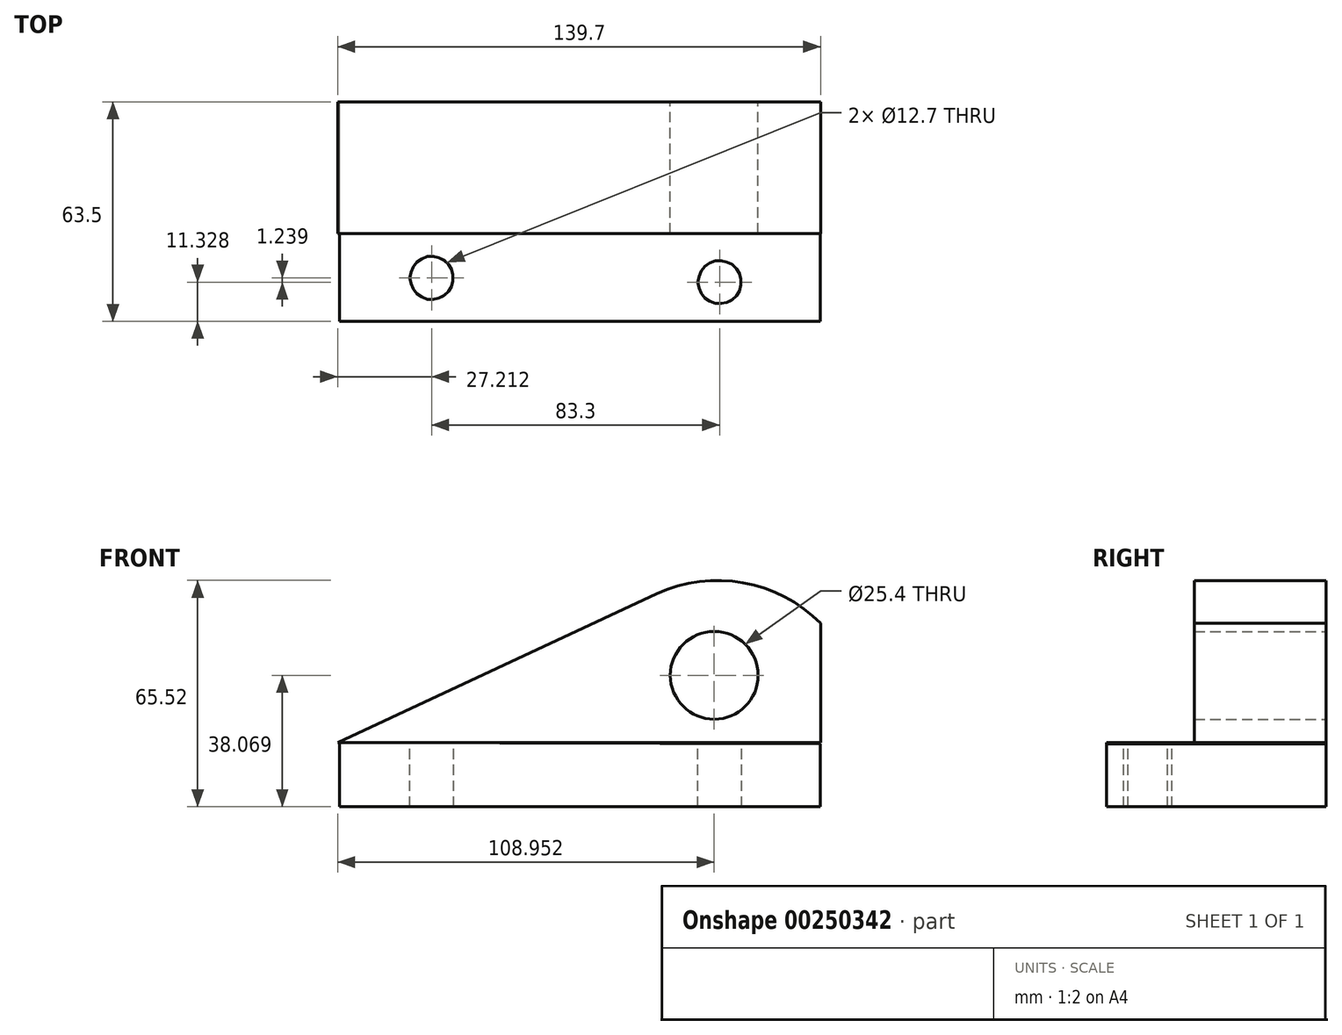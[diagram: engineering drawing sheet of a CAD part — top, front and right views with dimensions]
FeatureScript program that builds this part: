
annotation { "Feature Type Name" : "Feature", "Feature Type Description" : "" }
export const myFeature = defineFeature(function(context is Context, id is Id, definition is map)
    precondition{}
    {
        {
            var Q0;
            Q0=qCreatedBy(makeId("Front.planeOp"),FACE);
            var sketch = newSketch(context, id + "F0", { "sketchPlane" : qUnion([Q0])});
            skLineSegment(sketch, "E0", {"start": v(-73.3, -34.51) * mm, "end": v(66.4, -34.51) * mm});
            skLineSegment(sketch, "E1", {"start": v(66.4, -34.51) * mm, "end": v(66.4, 0) * mm});
            skLineSegment(sketch, "E2", {"start": v(-73.3, -34.51) * mm, "end": v(18.94, 8.51) * mm});
            skArc(sketch, "E3", {"start": v(66.4, 0) * mm, "mid": v(44.02, 11.78) * mm, "end": v(18.94, 8.51) * mm});
            skSolve(sketch);
        }
        {
            var Q0;
            Q0=qCreatedBy(makeId("Front.planeOp"),FACE);
            var sketch = newSketch(context, id + "F1", { "sketchPlane" : qUnion([Q0])});
            skLineSegment(sketch, "E4", {"start": v(66.3, -34.82) * mm, "end": v(66.3, -53.08) * mm});
            skLineSegment(sketch, "E5", {"start": v(66.3, -53.08) * mm, "end": v(-72.68, -53.08) * mm});
            skLineSegment(sketch, "E6", {"start": v(-72.68, -53.08) * mm, "end": v(-72.68, -34.51) * mm});
            skLineSegment(sketch, "E7", {"start": v(-72.68, -34.51) * mm, "end": v(66.3, -34.82) * mm});
            skSolve(sketch);
        }
        {
            var Q0;
            Q0=makeQuery(id+"F0.imprint","IMPRINT",FACE,{"disambiguationData":[TD([[makeQuery(id+"F0.imprint","IMPRINT",EDGE,{"derivedFrom":sQuery(id+"F0.wireOp",EDGE,"E0")}),1.0]])]});
            extrude(context, id + "F2", {"entities" : qUnion([Q0]), "depth" : 38.1 * mm});
        }
        {
            var Q0;
            Q0=makeQuery(id+"F1.imprint","IMPRINT",FACE,{"disambiguationData":[TD([[makeQuery(id+"F1.imprint","IMPRINT",EDGE,{"derivedFrom":sQuery(id+"F1.wireOp",EDGE,"E4")}),-1.0]])]});
            extrude(context, id + "F3", {"entities" : qUnion([Q0]), "depth" : 63.5 * mm});
        }
        {
            var Q0;
            Q0=qCreatedBy(makeId("Front.planeOp"),FACE);
            var sketch = newSketch(context, id + "F4", { "sketchPlane" : qUnion([Q0])});
            skLineSegment(sketch, "E8", {"start": v(35.65, -15.01) * mm, "end": v(10.9, -15.01) * mm});
            skSolve(sketch);
        }
        {
            var Q0;
            Q0=sQuery(id+"F4.wireOp",VERTEX,"E8.start");
            var Q1;
            Q1=makeQuery(id+"F2.opExtrude","SWEPT_BODY",BODY,{"disambiguationData":[OSD([sQuery(id+"F0.wireOp",EDGE,"E0"),sQuery(id+"F0.wireOp",EDGE,"E1"),sQuery(id+"F0.wireOp",EDGE,"E2"),sQuery(id+"F0.wireOp",EDGE,"E3")])]});
            hole(context, id + "F5", {"style" : HoleStyle.SIMPLE, "endStyle" : HoleEndStyle.THROUGH, "oppositeDirection" : true, "holeDiameter" : 25.4 * mm, "tappedDepth" : 12.7 * mm, "tapClearance" : 3, "locations" : qUnion([Q0]), "scope" : qUnion([Q1])});
        }
        {
            var Q0;
            Q0=qCreatedBy(makeId("Top.planeOp"),FACE);
            var sketch = newSketch(context, id + "F6", { "sketchPlane" : qUnion([Q0])});
            skLineSegment(sketch, "E9", {"start": v(-46.09, -50.93) * mm, "end": v(-64.98, -50.93) * mm});
            skSolve(sketch);
        }
        {
            var Q0;
            Q0=sQuery(id+"F6.wireOp",VERTEX,"E9.start");
            var Q1;
            Q1=makeQuery(id+"F3.opExtrude","SWEPT_BODY",BODY,{"disambiguationData":[OSD([sQuery(id+"F1.wireOp",EDGE,"E4"),sQuery(id+"F1.wireOp",EDGE,"E5"),sQuery(id+"F1.wireOp",EDGE,"E6"),sQuery(id+"F1.wireOp",EDGE,"E7")])]});
            hole(context, id + "F7", {"style" : HoleStyle.SIMPLE, "endStyle" : HoleEndStyle.THROUGH, "holeDiameter" : 12.7 * mm, "tappedDepth" : 12.7 * mm, "tapClearance" : 3, "locations" : qUnion([Q0]), "scope" : qUnion([Q1])});
        }
        {
            var Q0;
            Q0=qCreatedBy(makeId("Top.planeOp"),FACE);
            var sketch = newSketch(context, id + "F8", { "sketchPlane" : qUnion([Q0])});
            skLineSegment(sketch, "E10", {"start": v(37.21, -52.17) * mm, "end": v(20.5, -52.17) * mm});
            skSolve(sketch);
        }
        {
            var Q0;
            Q0=sQuery(id+"F8.wireOp",VERTEX,"E10.start");
            var Q1;
            Q1=makeQuery(id+"F3.opExtrude","SWEPT_BODY",BODY,{"disambiguationData":[OSD([sQuery(id+"F1.wireOp",EDGE,"E4"),sQuery(id+"F1.wireOp",EDGE,"E5"),sQuery(id+"F1.wireOp",EDGE,"E6"),sQuery(id+"F1.wireOp",EDGE,"E7")])]});
            hole(context, id + "F9", {"style" : HoleStyle.SIMPLE, "endStyle" : HoleEndStyle.THROUGH, "holeDiameter" : 12.7 * mm, "tappedDepth" : 12.7 * mm, "tapClearance" : 3, "locations" : qUnion([Q0]), "scope" : qUnion([Q1])});
        }
    });
